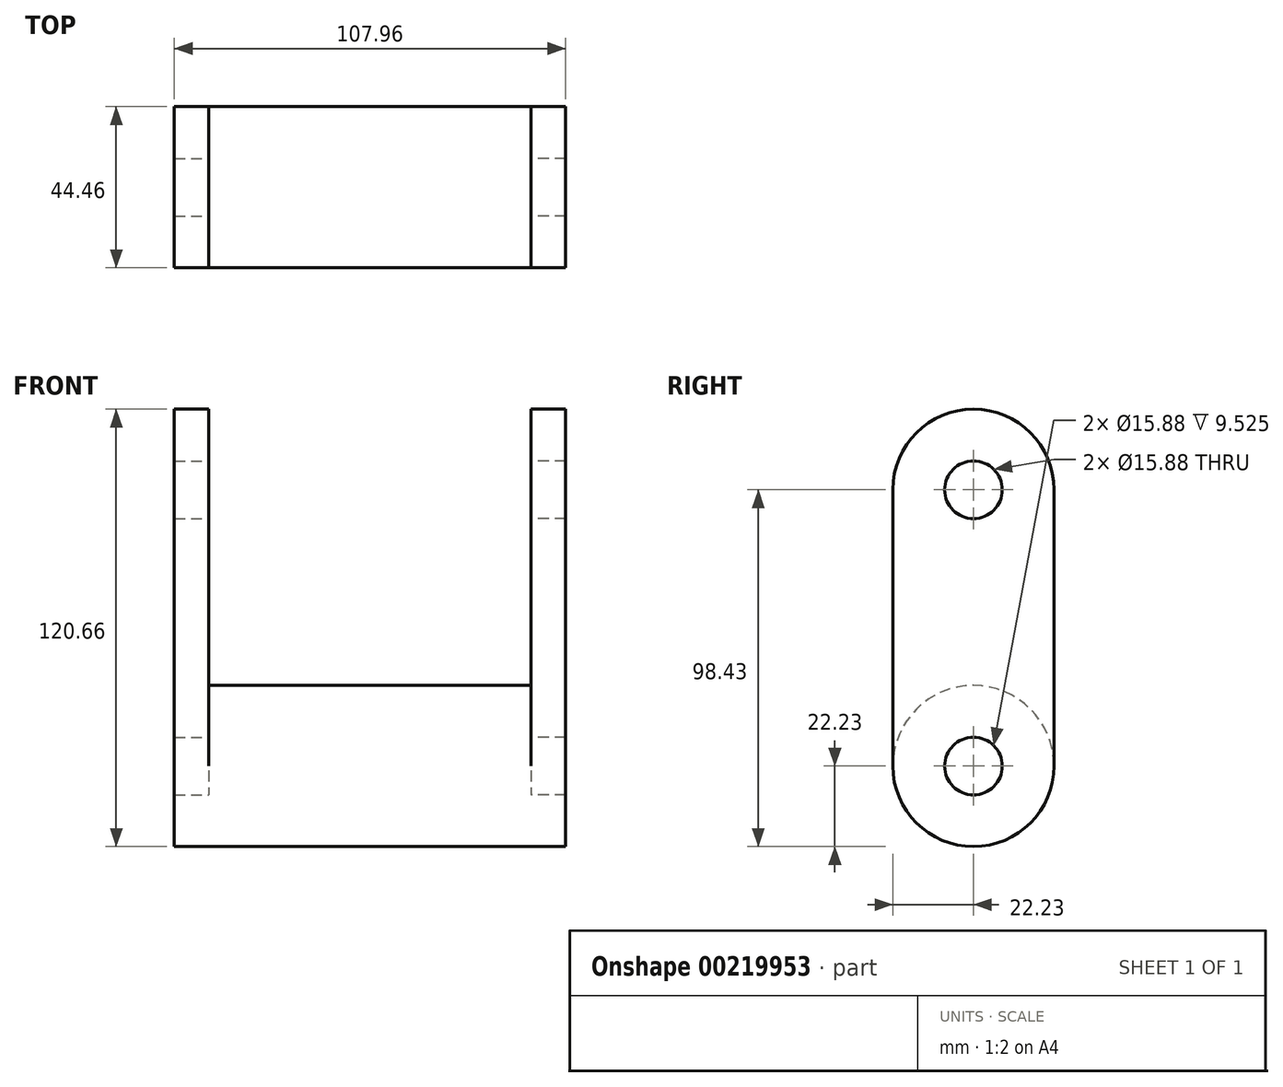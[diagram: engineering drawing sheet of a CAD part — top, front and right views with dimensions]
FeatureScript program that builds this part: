
annotation { "Feature Type Name" : "Feature", "Feature Type Description" : "" }
export const myFeature = defineFeature(function(context is Context, id is Id, definition is map)
    precondition{}
    {
        {
            var Q0;
            Q0=qCreatedBy(makeId("Right.planeOp"),FACE);
            var sketch = newSketch(context, id + "F0", { "sketchPlane" : qUnion([Q0])});
            skCircle(sketch, "E0", {"center": v(0, 0) * mm, "radius": 22.23 * mm});
            skSolve(sketch);
        }
        {
            var Q0;
            Q0 = qSketchRegion(id + "F0", true);
            extrude(context, id + "F1", {"entities" : qUnion([Q0]), "endBound" : BoundingType.SYMMETRIC, "depth" : 88.9 * mm});
        }
        {
            var Q0;
            Q0=makeQuery(id+"F1.opExtrude","CAP_FACE",FACE,{"disambiguationData":[OSD([sQuery(id+"F0.wireOp",EDGE,"E0")])],"isStart":true});
            var sketch = newSketch(context, id + "F2", { "sketchPlane" : qUnion([Q0])});
            skArc(sketch, "E1.0.0", {"start": v(-22.23, 0) * mm, "mid": v(0, -22.23) * mm, "end": v(22.23, 0) * mm});
            skLineSegment(sketch, "E2", {"start": v(-22.23, 0) * mm, "end": v(22.23, 0) * mm, "construction": true});
            skLineSegment(sketch, "E3", {"start": v(-22.23, 0) * mm, "end": v(-22.23, 76.2) * mm});
            skLineSegment(sketch, "E4", {"start": v(-22.23, 76.2) * mm, "end": v(22.23, 76.2) * mm, "construction": true});
            skLineSegment(sketch, "E5", {"start": v(22.23, 76.2) * mm, "end": v(22.23, 0) * mm});
            skArc(sketch, "E6", {"start": v(22.23, 76.2) * mm, "mid": v(0, 98.43) * mm, "end": v(-22.23, 76.2) * mm});
            skCircle(sketch, "E7", {"center": v(0, 76.2) * mm, "radius": 7.94 * mm});
            skCircle(sketch, "E8", {"center": v(0, 0) * mm, "radius": 7.94 * mm});
            skSolve(sketch);
        }
        {
            var Q0;
            Q0 = qSketchRegion(id + "F2", true);
            extrude(context, id + "F3", {"entities" : qUnion([Q0]), "operationType" : NewBodyOperationType.ADD, "depth" : 9.52 * mm});
        }
        {
            var Q0;
            Q0=makeQuery(id+"F1.opExtrude","SWEPT_BODY",BODY,{"disambiguationData":[OSD([sQuery(id+"F0.wireOp",EDGE,"E0")])]});
            var Q1;
            Q1=qCreatedBy(makeId("Right.planeOp"),FACE);
            mirror(context, id + "F4", {"operationType" : NewBodyOperationType.ADD, "entities" : qUnion([Q0]), "mirrorPlane" : qUnion([Q1])});
        }
    });
